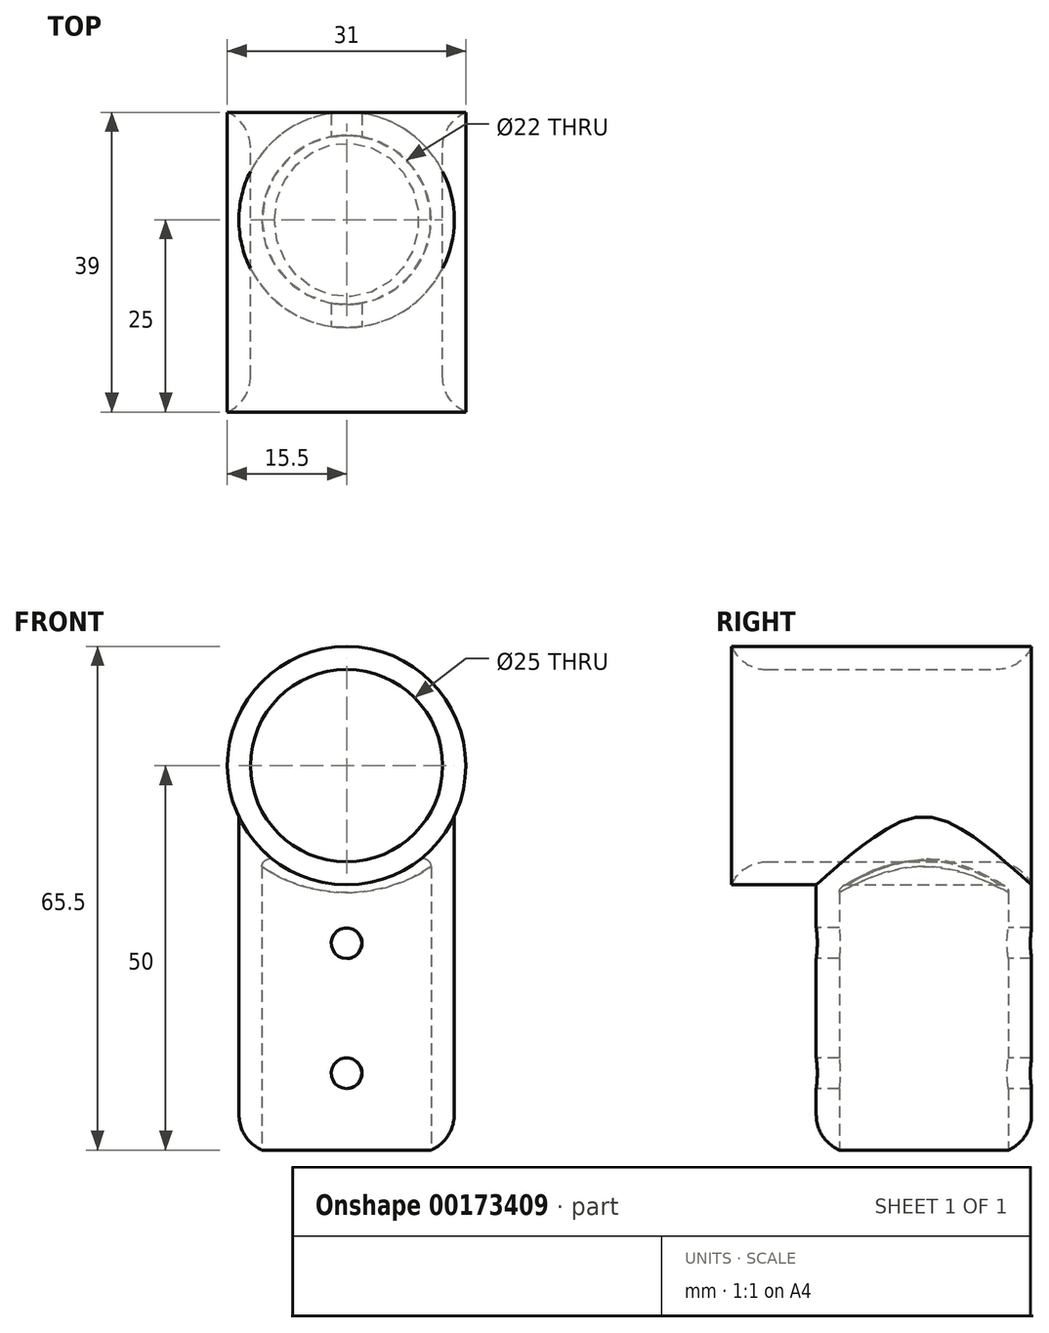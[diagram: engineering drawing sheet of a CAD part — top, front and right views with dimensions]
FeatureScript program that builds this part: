
annotation { "Feature Type Name" : "Feature", "Feature Type Description" : "" }
export const myFeature = defineFeature(function(context is Context, id is Id, definition is map)
    precondition{}
    {
        {
            var Q0;
            Q0=qCreatedBy(makeId("Top.planeOp"),FACE);
            var sketch = newSketch(context, id + "F0", { "sketchPlane" : qUnion([Q0])});
            skCircle(sketch, "E0", {"center": v(0, 0) * mm, "radius": 11 * mm});
            skCircle(sketch, "E1", {"center": v(0, 0) * mm, "radius": 14 * mm});
            skSolve(sketch);
        }
        {
            var Q0;
            Q0=qSketchRegion(id+"F0",true);
            extrude(context, id + "F1", {"entities" : qUnion([Q0]), "depth" : 40 * mm, "hasSecondDirection" : true, "secondDirectionOppositeDirection" : true, "secondDirectionDepth" : 10 * mm});
        }
        {
            var Q0;
            Q0=qCreatedBy(makeId("Front.planeOp"),FACE);
            var sketch = newSketch(context, id + "F2", { "sketchPlane" : qUnion([Q0])});
            skCircle(sketch, "E2", {"center": v(0, 40) * mm, "radius": 12.5 * mm});
            skCircle(sketch, "E3", {"center": v(0, 40) * mm, "radius": 15.5 * mm});
            skSolve(sketch);
        }
        {
            var Q0;
            Q0=makeQuery(id+"F2.imprint","IMPRINT",FACE,{"disambiguationData":[TD([[makeQuery(id+"F2.imprint","IMPRINT",EDGE,{"derivedFrom":sQuery(id+"F2.wireOp",EDGE,"E2")}),-1.0]])]});
            extrude(context, id + "F3", {"entities" : qUnion([Q0]), "operationType" : NewBodyOperationType.ADD, "depth" : 25 * mm, "hasSecondDirection" : true, "secondDirectionOppositeDirection" : true, "secondDirectionDepth" : 14 * mm});
        }
        {
            var Q0;
            Q0=makeQuery(id+"F2.imprint","IMPRINT",FACE,{"disambiguationData":[TD([[makeQuery(id+"F2.imprint","IMPRINT",EDGE,{"derivedFrom":sQuery(id+"F2.wireOp",EDGE,"E2")}),1.0]])]});
            extrude(context, id + "F4", {"entities" : qUnion([Q0]), "operationType" : NewBodyOperationType.REMOVE, "oppositeDirection" : true, "depth" : 25 * mm, "hasSecondDirection" : true, "secondDirectionOppositeDirection" : false, "secondDirectionDepth" : 25 * mm});
        }
        {
            var Q0;
            Q0=qCreatedBy(makeId("Front.planeOp"),FACE);
            var sketch = newSketch(context, id + "F5", { "sketchPlane" : qUnion([Q0])});
            skCircle(sketch, "E4", {"center": v(0, 16.9) * mm, "radius": 2 * mm});
            skCircle(sketch, "E5", {"center": v(0, 0) * mm, "radius": 2 * mm});
            skSolve(sketch);
        }
        {
            var Q0;
            Q0=qSketchRegion(id+"F5",true);
            extrude(context, id + "F6", {"entities" : qUnion([Q0]), "operationType" : NewBodyOperationType.REMOVE, "oppositeDirection" : true, "depth" : 25 * mm, "hasSecondDirection" : true, "secondDirectionOppositeDirection" : false, "secondDirectionDepth" : 25 * mm});
        }
        {
            var Q0;
            Q0=makeQuery(id+"F3.opExtrude","CAP_EDGE",EDGE,{"disambiguationData":[OSD([sQuery(id+"F2.wireOp",EDGE,"E2")])],"isStart":true});
            var Q1;
            Q1=makeQuery(id+"F3.opExtrude","CAP_EDGE",EDGE,{"disambiguationData":[OSD([sQuery(id+"F2.wireOp",EDGE,"E2")])],"isStart":false});
            var Q2;
            Q2=makeQuery(id+"F1.opExtrude","CAP_EDGE",EDGE,{"disambiguationData":[OSD([sQuery(id+"F0.wireOp",EDGE,"E1")])],"isStart":true});
            fillet(context, id + "F7", {"entities" : qUnion([Q0, Q1, Q2]), "radius" : 5 * mm, "tangentPropagation" : true, "allowEdgeOverflow" : false});
        }
        {
            var Q0;
            Q0=makeQuery(id+"F3.boolean.opBoolean","INTERSECT",EDGE,{"derivedFrom":[makeQuery(id+"F1.opExtrude","SWEPT_FACE",FACE,{"disambiguationData":[OSD([sQuery(id+"F0.wireOp",EDGE,"E0")])]}),makeQuery(id+"F3.opExtrude","SWEPT_FACE",FACE,{"disambiguationData":[OSD([sQuery(id+"F2.wireOp",EDGE,"E3")])]})]});
            fillet(context, id + "F8", {"entities" : qUnion([Q0]), "radius" : 1 * mm, "tangentPropagation" : true, "allowEdgeOverflow" : false});
        }
    });
